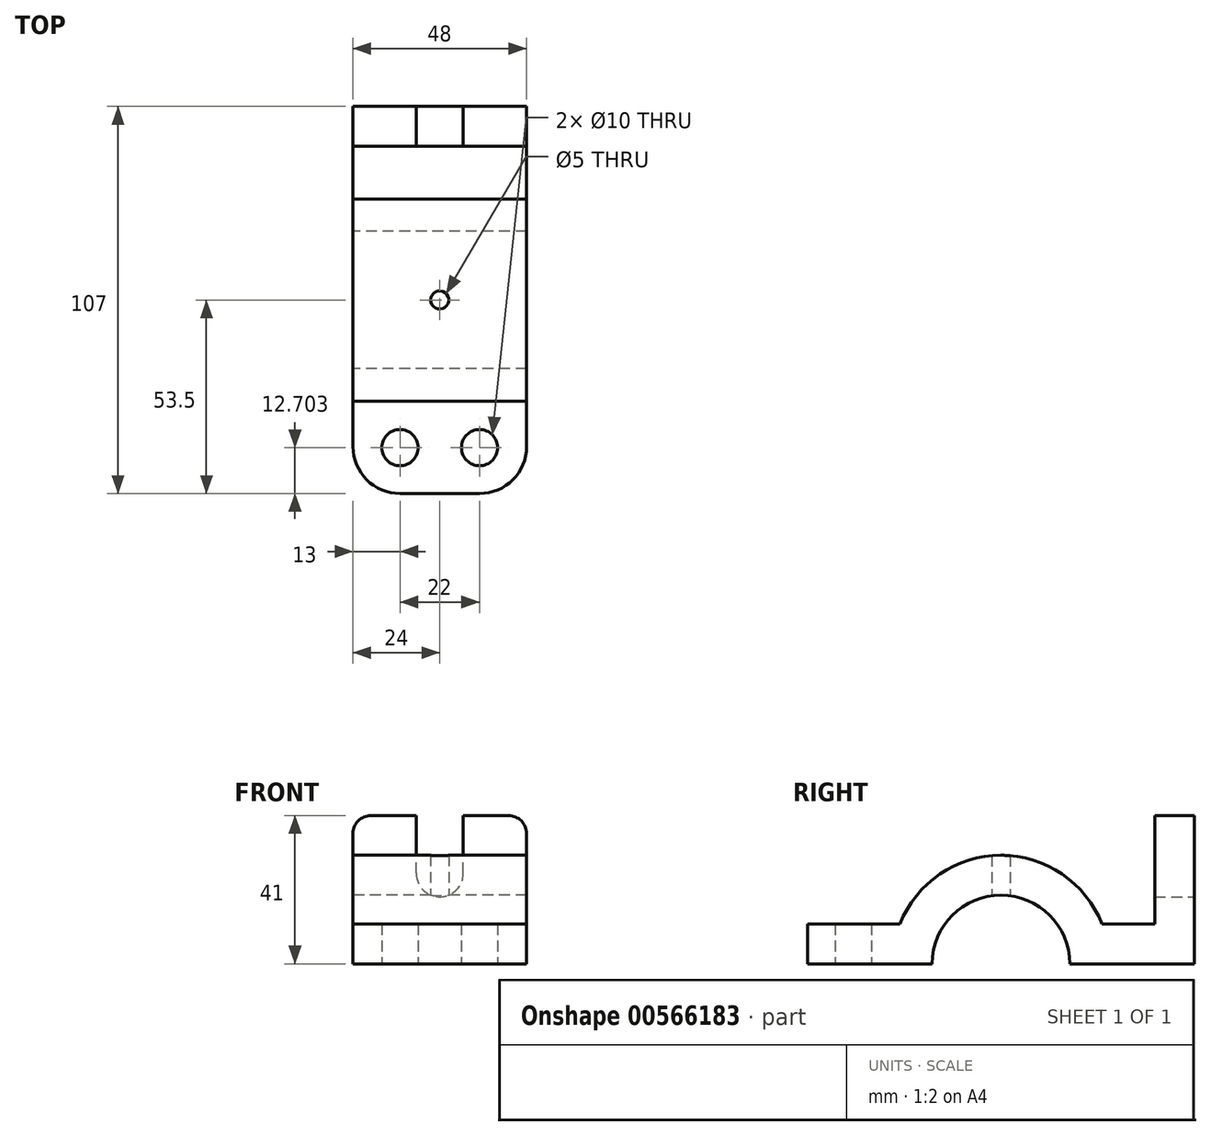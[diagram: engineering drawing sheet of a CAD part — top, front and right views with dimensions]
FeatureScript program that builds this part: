
annotation { "Feature Type Name" : "Feature", "Feature Type Description" : "" }
export const myFeature = defineFeature(function(context is Context, id is Id, definition is map)
    precondition{}
    {
        {
            var Q0;
            Q0=qCreatedBy(makeId("Right.planeOp"),FACE);
            var sketch = newSketch(context, id + "F0", { "sketchPlane" : qUnion([Q0])});
            skArc(sketch, "E0", {"start": v(19, 0) * mm, "mid": v(0, 19) * mm, "end": v(-19, 0) * mm});
            skLineSegment(sketch, "E1", {"start": v(-19, 0) * mm, "end": v(-53.5, 0) * mm});
            skLineSegment(sketch, "E2.bottom", {"start": v(-53.5, 0) * mm, "end": v(-19, 0) * mm});
            skLineSegment(sketch, "E2.top", {"start": v(-53.5, 11) * mm, "end": v(-27.91, 11) * mm});
            skLineSegment(sketch, "E2.left", {"start": v(-53.5, 0) * mm, "end": v(-53.5, 11) * mm});
            skLineSegment(sketch, "E2.right", {"start": v(53.5, 0) * mm, "end": v(53.5, 11) * mm});
            skLineSegment(sketch, "E3.top", {"start": v(53.5, 41) * mm, "end": v(42.5, 41) * mm});
            skLineSegment(sketch, "E3.left", {"start": v(53.5, 11) * mm, "end": v(53.5, 41) * mm});
            skLineSegment(sketch, "E3.right", {"start": v(42.5, 11) * mm, "end": v(42.5, 41) * mm});
            skLineSegment(sketch, "E4.trimOffspring", {"start": v(27.91, 11) * mm, "end": v(42.5, 11) * mm});
            skArc(sketch, "E5.trimOffspring", {"start": v(27.91, 11) * mm, "mid": v(0, 30) * mm, "end": v(-27.91, 11) * mm});
            skLineSegment(sketch, "E6.trimOffspring", {"start": v(19, 0) * mm, "end": v(53.5, 0) * mm});
            skSolve(sketch);
        }
        {
            var Q0;
            {var subQ0=sQuery(id+"F0.wireOp",EDGE,"E2.top");var subQ1=sQuery(id+"F0.wireOp",EDGE,"tjlXP0vc-IT0C-k8YI-ZeuR-Yf8jVUY6XKPl");var subQ2=makeQuery(id+"F0.imprint","INTERSECT",VERTEX,{"disambiguationData":[OD(0.0)],"derivedFrom":[subQ1,subQ0]});Q0=makeQuery(id+"F0.imprint","IMPRINT",FACE,{"disambiguationData":[TD([[makeQuery(id+"F0.imprint","IMPRINT",EDGE,{"disambiguationData":[TD([[subQ2,-1.0]])],"derivedFrom":subQ1}),1.0]])]});}
            var Q1;
            {var subQ5=sQuery(id+"F0.wireOp",EDGE,"E2.left");Q1=makeQuery(id+"F0.imprint","IMPRINT",FACE,{"disambiguationData":[TD([[makeQuery(id+"F0.imprint","IMPRINT",EDGE,{"derivedFrom":subQ5}),-1.0]])]});}
            var Q2;
            Q2=makeQuery(id+"F0.imprint","IMPRINT",FACE,{"disambiguationData":[TD([[makeQuery(id+"F0.imprint","IMPRINT",EDGE,{"derivedFrom":sQuery(id+"F0.wireOp",EDGE,"E3.bottom")}),-1.0]])]});
            var Q3;
            {var subQ4=sQuery(id+"F0.wireOp",EDGE,"E2.right");Q3=makeQuery(id+"F0.imprint","IMPRINT",FACE,{"disambiguationData":[TD([[makeQuery(id+"F0.imprint","IMPRINT",EDGE,{"derivedFrom":subQ4}),1.0]])]});}
            var Q4;
            {var subQ3=sQuery(id+"F0.wireOp",EDGE,"E2.bottom");var subQ5=sQuery(id+"F0.wireOp",EDGE,"E0");var subQ6=makeQuery(id+"F0.imprint","INTERSECT",VERTEX,{"disambiguationData":[OD(0.0)],"derivedFrom":[subQ5,subQ3]});Q4=makeQuery(id+"F0.imprint","IMPRINT",FACE,{"disambiguationData":[TD([[makeQuery(id+"F0.imprint","IMPRINT",EDGE,{"disambiguationData":[TD([[subQ6,1.0]])],"derivedFrom":subQ5}),-1.0]])]});}
            extrude(context, id + "F1", {"entities" : qUnion([Q0, Q1, Q2, Q3, Q4]), "endBound" : BoundingType.SYMMETRIC, "depth" : 48 * mm, "offsetDistance" : 25 * mm});
        }
        {
            var Q0;
            Q0=makeQuery(id+"F1.opExtrude","SWEPT_FACE",FACE,{"disambiguationData":[OSD([sQuery(id+"F0.wireOp",EDGE,"E2.right"),sQuery(id+"F0.wireOp",EDGE,"E3.left")])]});
            var sketch = newSketch(context, id + "F2", { "sketchPlane" : qUnion([Q0])});
            skArc(sketch, "E7", {"start": v(-6.5, 25.04) * mm, "mid": v(0, 18.5) * mm, "end": v(6.5, 25.04) * mm});
            skLineSegment(sketch, "E8", {"start": v(-6.5, 25.04) * mm, "end": v(-6.5, 41) * mm});
            skLineSegment(sketch, "E9", {"start": v(6.5, 25.04) * mm, "end": v(6.5, 41) * mm});
            skSolve(sketch);
        }
        {
            var Q0;
            Q0=makeQuery(id+"F1.opExtrude","CAP_EDGE",EDGE,{"disambiguationData":[OSD([sQuery(id+"F0.wireOp",EDGE,"E2.left")])],"isStart":true});
            var Q1;
            Q1=makeQuery(id+"F1.opExtrude","CAP_EDGE",EDGE,{"disambiguationData":[OSD([sQuery(id+"F0.wireOp",EDGE,"E2.left")])],"isStart":false});
            fillet(context, id + "F3", {"entities" : qUnion([Q0, Q1]), "radius" : 13 * mm, "tangentPropagation" : true, "allowEdgeOverflow" : false});
        }
        {
            var Q0;
            Q0=makeQuery(id+"F1.opExtrude","CAP_EDGE",EDGE,{"disambiguationData":[OSD([sQuery(id+"F0.wireOp",EDGE,"E3.top")])],"isStart":true});
            var Q1;
            Q1=makeQuery(id+"F1.opExtrude","CAP_EDGE",EDGE,{"disambiguationData":[OSD([sQuery(id+"F0.wireOp",EDGE,"E3.top")])],"isStart":false});
            fillet(context, id + "F4", {"entities" : qUnion([Q0, Q1]), "radius" : 5 * mm, "tangentPropagation" : true, "allowEdgeOverflow" : false});
        }
        {
            var Q0;
            Q0=qCreatedBy(makeId("Top.planeOp"),FACE);
            var sketch = newSketch(context, id + "F5", { "sketchPlane" : qUnion([Q0])});
            skLineSegment(sketch, "E10", {"start": v(-22.37, -40.8) * mm, "end": v(25.63, -40.8) * mm, "construction": true});
            skLineSegment(sketch, "E11", {"start": v(0, -27.86) * mm, "end": v(0, -53.73) * mm, "construction": true});
            skCircle(sketch, "E12", {"center": v(-11, -40.8) * mm, "radius": 5 * mm});
            skCircle(sketch, "E13", {"center": v(11, -40.8) * mm, "radius": 5 * mm});
            skPoint(sketch, "E14", {"position": v(0, -40.8) * mm});
            skCircle(sketch, "E15", {"center": v(0, 0) * mm, "radius": 2.5 * mm});
            skSolve(sketch);
        }
        {
            var Q0;
            Q0=makeQuery(id+"F2.imprint","IMPRINT",FACE,{"disambiguationData":[TD([[makeQuery(id+"F2.imprint","IMPRINT",EDGE,{"derivedFrom":sQuery(id+"F2.wireOp",EDGE,"E7")}),1.0]])]});
            extrude(context, id + "F6", {"entities" : qUnion([Q0]), "operationType" : NewBodyOperationType.REMOVE, "endBound" : BoundingType.UP_TO_NEXT, "oppositeDirection" : true, "depth" : 25 * mm, "offsetDistance" : 25 * mm});
        }
        {
            var Q0;
            Q0=makeQuery(id+"F5.imprint","IMPRINT",FACE,{"disambiguationData":[TD([[makeQuery(id+"F5.imprint","IMPRINT",EDGE,{"derivedFrom":sQuery(id+"F5.wireOp",EDGE,"E12")}),1.0]])]});
            var Q1;
            Q1=makeQuery(id+"F5.imprint","IMPRINT",FACE,{"disambiguationData":[TD([[makeQuery(id+"F5.imprint","IMPRINT",EDGE,{"derivedFrom":sQuery(id+"F5.wireOp",EDGE,"E13")}),1.0]])]});
            var Q2;
            Q2=makeQuery(id+"F5.imprint","IMPRINT",FACE,{"disambiguationData":[TD([[makeQuery(id+"F5.imprint","IMPRINT",EDGE,{"derivedFrom":sQuery(id+"F5.wireOp",EDGE,"E15")}),1.0]])]});
            extrude(context, id + "F7", {"entities" : qUnion([Q0, Q1, Q2]), "operationType" : NewBodyOperationType.REMOVE, "endBound" : BoundingType.THROUGH_ALL, "depth" : 25 * mm, "offsetDistance" : 25 * mm});
        }
    });
